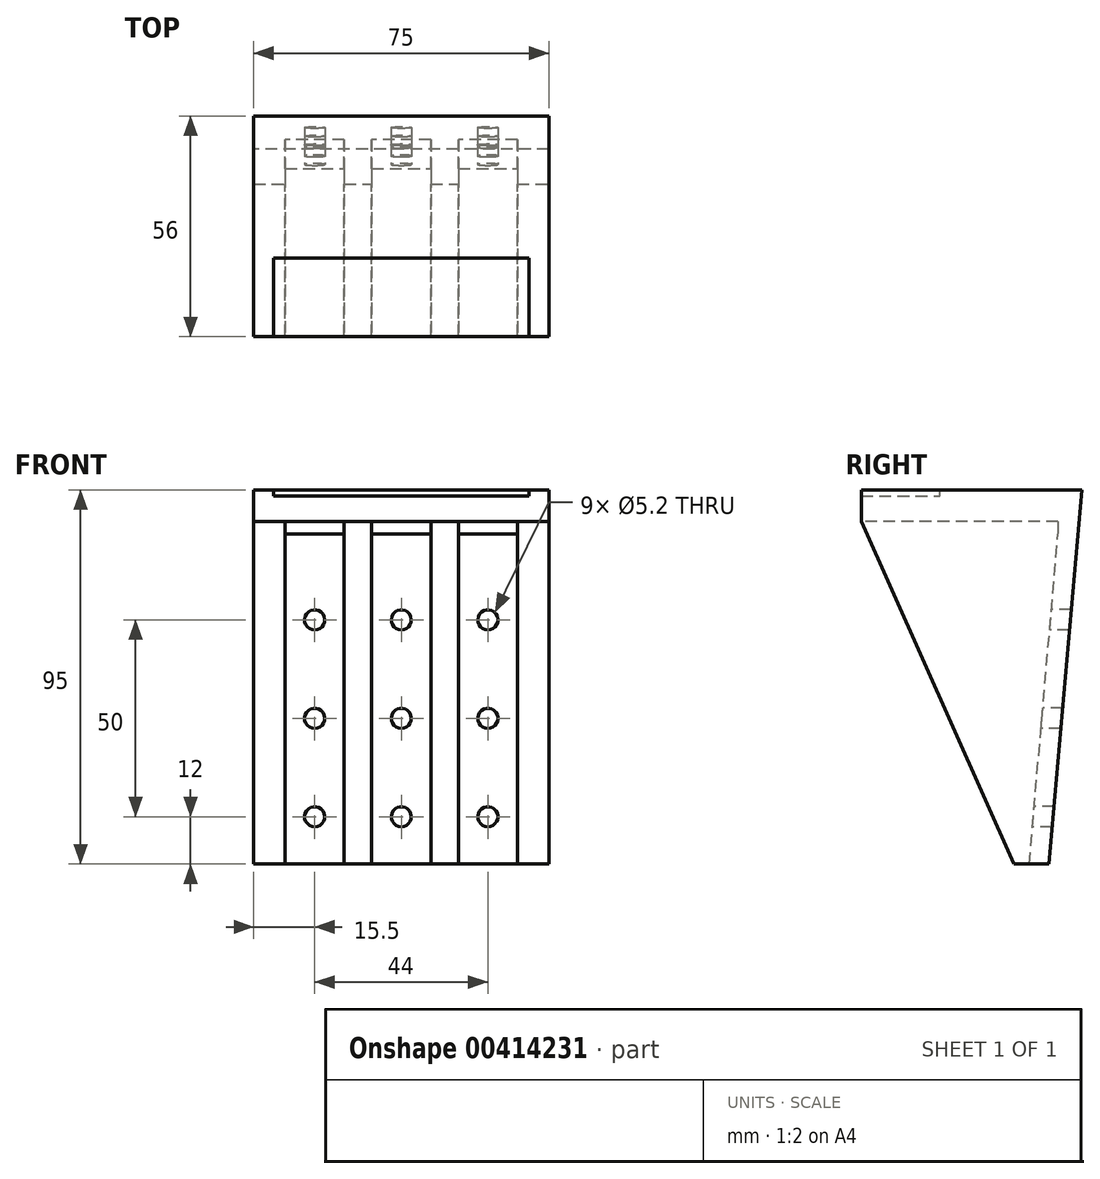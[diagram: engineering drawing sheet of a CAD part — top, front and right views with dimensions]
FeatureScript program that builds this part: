
annotation { "Feature Type Name" : "Feature", "Feature Type Description" : "" }
export const myFeature = defineFeature(function(context is Context, id is Id, definition is map)
    precondition{}
    {
        {
            var Q0;
            Q0=qCreatedBy(makeId("Front.planeOp"),FACE);
            var sketch = newSketch(context, id + "F0", { "sketchPlane" : qUnion([Q0])});
            skLineSegment(sketch, "E0.bottom", {"start": v(0, 0) * mm, "end": v(75, 0) * mm});
            skLineSegment(sketch, "E0.top", {"start": v(0, 100) * mm, "end": v(75, 100) * mm});
            skLineSegment(sketch, "E0.left", {"start": v(0, 0) * mm, "end": v(0, 100) * mm});
            skLineSegment(sketch, "E0.right", {"start": v(75, 0) * mm, "end": v(75, 100) * mm});
            skSolve(sketch);
        }
        {
            var Q0;
            Q0=makeQuery(id+"F0.imprint","IMPRINT",FACE,{"disambiguationData":[TD([[makeQuery(id+"F0.imprint","IMPRINT",EDGE,{"derivedFrom":sQuery(id+"F0.wireOp",EDGE,"E0.bottom")}),1.0]])]});
            extrude(context, id + "F1", {"entities" : qUnion([Q0]), "depth" : 56 * mm});
        }
        {
            var Q0;
            Q0=makeQuery(id+"F1.opExtrude","SWEPT_FACE",FACE,{"disambiguationData":[OSD([sQuery(id+"F0.wireOp",EDGE,"E0.left")])]});
            var sketch = newSketch(context, id + "F2", { "sketchPlane" : qUnion([Q0])});
            skLineSegment(sketch, "E1", {"start": v(15, 0) * mm, "end": v(56, 92) * mm});
            skLineSegment(sketch, "E2", {"start": v(56, 92) * mm, "end": v(56, 0) * mm});
            skLineSegment(sketch, "E3", {"start": v(56, 0) * mm, "end": v(15, 0) * mm});
            skSolve(sketch);
        }
        {
            var Q0;
            Q0=makeQuery(id+"F2.imprint","IMPRINT",FACE,{"disambiguationData":[TD([[makeQuery(id+"F2.imprint","IMPRINT",EDGE,{"derivedFrom":sQuery(id+"F2.wireOp",EDGE,"E1")}),-1.0]])]});
            extrude(context, id + "F3", {"entities" : qUnion([Q0]), "operationType" : NewBodyOperationType.REMOVE, "endBound" : BoundingType.THROUGH_ALL, "oppositeDirection" : true, "depth" : 25 * mm});
        }
        {
            var Q0;
            Q0=makeQuery(id+"F1.opExtrude","CAP_FACE",FACE,{"disambiguationData":[OSD([sQuery(id+"F0.wireOp",EDGE,"E0.bottom"),sQuery(id+"F0.wireOp",EDGE,"E0.top"),sQuery(id+"F0.wireOp",EDGE,"E0.left"),sQuery(id+"F0.wireOp",EDGE,"E0.right")])],"isStart":false});
            var sketch = newSketch(context, id + "F4", { "sketchPlane" : qUnion([Q0])});
            skLineSegment(sketch, "E4.bottom", {"start": v(8, 92) * mm, "end": v(23, 92) * mm});
            skLineSegment(sketch, "E4.top", {"start": v(8, 0) * mm, "end": v(23, 0) * mm});
            skLineSegment(sketch, "E4.left", {"start": v(8, 92) * mm, "end": v(8, 0) * mm});
            skLineSegment(sketch, "E4.right", {"start": v(23, 92) * mm, "end": v(23, 0) * mm});
            skLineSegment(sketch, "E5.bottom", {"start": v(30, 92) * mm, "end": v(45, 92) * mm});
            skLineSegment(sketch, "E5.top", {"start": v(30, 0) * mm, "end": v(45, 0) * mm});
            skLineSegment(sketch, "E5.left", {"start": v(30, 92) * mm, "end": v(30, 0) * mm});
            skLineSegment(sketch, "E5.right", {"start": v(45, 92) * mm, "end": v(45, 0) * mm});
            skLineSegment(sketch, "E6.bottom", {"start": v(52, 92) * mm, "end": v(67, 92) * mm});
            skLineSegment(sketch, "E6.top", {"start": v(52, 0) * mm, "end": v(67, 0) * mm});
            skLineSegment(sketch, "E6.left", {"start": v(52, 92) * mm, "end": v(52, 0) * mm});
            skLineSegment(sketch, "E6.right", {"start": v(67, 92) * mm, "end": v(67, 0) * mm});
            skSolve(sketch);
        }
        {
            var Q0;
            Q0=makeQuery(id+"F4.imprint","IMPRINT",FACE,{"disambiguationData":[TD([[makeQuery(id+"F4.imprint","IMPRINT",EDGE,{"derivedFrom":sQuery(id+"F4.wireOp",EDGE,"E4.bottom")}),1.0]])]});
            var Q1;
            Q1=makeQuery(id+"F4.imprint","IMPRINT",FACE,{"disambiguationData":[TD([[makeQuery(id+"F4.imprint","IMPRINT",EDGE,{"derivedFrom":sQuery(id+"F4.wireOp",EDGE,"E5.bottom")}),1.0]])]});
            var Q2;
            Q2=makeQuery(id+"F4.imprint","IMPRINT",FACE,{"disambiguationData":[TD([[makeQuery(id+"F4.imprint","IMPRINT",EDGE,{"derivedFrom":sQuery(id+"F4.wireOp",EDGE,"E6.bottom")}),1.0]])]});
            extrude(context, id + "F5", {"entities" : qUnion([Q0, Q1, Q2]), "operationType" : NewBodyOperationType.REMOVE, "oppositeDirection" : true, "depth" : 50 * mm});
        }
        {
            var Q0;
            Q0=makeQuery(id+"F1.opExtrude","SWEPT_FACE",FACE,{"disambiguationData":[OSD([sQuery(id+"F0.wireOp",EDGE,"E0.top")])]});
            var sketch = newSketch(context, id + "F6", { "sketchPlane" : qUnion([Q0])});
            skLineSegment(sketch, "E7.bottom", {"start": v(5, -56) * mm, "end": v(70, -56) * mm});
            skLineSegment(sketch, "E7.top", {"start": v(5, -36) * mm, "end": v(70, -36) * mm});
            skLineSegment(sketch, "E7.left", {"start": v(5, -56) * mm, "end": v(5, -36) * mm});
            skLineSegment(sketch, "E7.right", {"start": v(70, -56) * mm, "end": v(70, -36) * mm});
            skSolve(sketch);
        }
        {
            var Q0;
            Q0=makeQuery(id+"F6.imprint","IMPRINT",FACE,{"disambiguationData":[TD([[makeQuery(id+"F6.imprint","IMPRINT",EDGE,{"derivedFrom":sQuery(id+"F6.wireOp",EDGE,"E7.bottom")}),1.0]])]});
            extrude(context, id + "F7", {"entities" : qUnion([Q0]), "operationType" : NewBodyOperationType.REMOVE, "oppositeDirection" : true, "depth" : 1.5 * mm});
        }
        {
            var Q0;
            Q0=makeQuery(id+"F1.opExtrude","SWEPT_FACE",FACE,{"disambiguationData":[OSD([sQuery(id+"F0.wireOp",EDGE,"E0.left")])]});
            var sketch = newSketch(context, id + "F8", { "sketchPlane" : qUnion([Q0])});
            skLineSegment(sketch, "E8", {"start": v(0, 100) * mm, "end": v(8.75, 0) * mm});
            skLineSegment(sketch, "E9", {"start": v(8.75, 0) * mm, "end": v(0, 0) * mm});
            skLineSegment(sketch, "E10", {"start": v(0, 0) * mm, "end": v(0, 100) * mm});
            skSolve(sketch);
        }
        {
            var Q0;
            Q0=makeQuery(id+"F8.imprint","IMPRINT",FACE,{"disambiguationData":[TD([[makeQuery(id+"F8.imprint","IMPRINT",EDGE,{"derivedFrom":sQuery(id+"F8.wireOp",EDGE,"E8")}),-1.0]])]});
            extrude(context, id + "F9", {"entities" : qUnion([Q0]), "operationType" : NewBodyOperationType.REMOVE, "endBound" : BoundingType.THROUGH_ALL, "oppositeDirection" : true, "depth" : 25 * mm});
        }
        {
            var Q0;
            Q0=makeQuery(id+"F1.opExtrude","SWEPT_FACE",FACE,{"disambiguationData":[OSD([sQuery(id+"F0.wireOp",EDGE,"E0.left")])]});
            var sketch = newSketch(context, id + "F10", { "sketchPlane" : qUnion([Q0])});
            skLineSegment(sketch, "E11", {"start": v(0, 100) * mm, "end": v(8.75, 0) * mm});
            skLineSegment(sketch, "E12", {"start": v(8.75, 0) * mm, "end": v(13.77, 0) * mm});
            skLineSegment(sketch, "E13", {"start": v(13.77, 0) * mm, "end": v(5.02, 100) * mm});
            skLineSegment(sketch, "E14", {"start": v(5.02, 100) * mm, "end": v(0, 100) * mm});
            skSolve(sketch);
        }
        {
            var Q0;
            Q0=makeQuery(id+"F10.imprint","IMPRINT",FACE,{"disambiguationData":[TD([[makeQuery(id+"F10.imprint","IMPRINT",EDGE,{"derivedFrom":sQuery(id+"F10.wireOp",EDGE,"E11")}),1.0]])]});
            var Q1;
            Q1=makeQuery(id+"F1.opExtrude","SWEPT_FACE",FACE,{"disambiguationData":[OSD([sQuery(id+"F0.wireOp",EDGE,"E0.right")])]});
            extrude(context, id + "F11", {"entities" : qUnion([Q0]), "operationType" : NewBodyOperationType.ADD, "endBound" : BoundingType.UP_TO_SURFACE, "oppositeDirection" : true, "endBoundEntityFace" : qUnion([Q1]), "depth" : 25 * mm});
        }
        {
            var Q0;
            Q0=makeQuery(id+"F1.opExtrude","CAP_FACE",FACE,{"disambiguationData":[OSD([sQuery(id+"F0.wireOp",EDGE,"E0.bottom"),sQuery(id+"F0.wireOp",EDGE,"E0.top"),sQuery(id+"F0.wireOp",EDGE,"E0.left"),sQuery(id+"F0.wireOp",EDGE,"E0.right")])],"isStart":false});
            var sketch = newSketch(context, id + "F12", { "sketchPlane" : qUnion([Q0])});
            skLineSegment(sketch, "E15", {"start": v(15.5, 92) * mm, "end": v(15.5, 0) * mm, "construction": true});
            skLineSegment(sketch, "E16", {"start": v(37.5, 92) * mm, "end": v(37.5, 0) * mm, "construction": true});
            skLineSegment(sketch, "E17", {"start": v(59.5, 92) * mm, "end": v(59.5, 0) * mm, "construction": true});
            skLineSegment(sketch, "E18.bottom", {"start": v(0, 0) * mm, "end": v(75, 0) * mm});
            skLineSegment(sketch, "E18.top", {"start": v(0, 5) * mm, "end": v(75, 5) * mm});
            skLineSegment(sketch, "E18.left", {"start": v(0, 0) * mm, "end": v(0, 5) * mm});
            skLineSegment(sketch, "E18.right", {"start": v(75, 0) * mm, "end": v(75, 5) * mm});
            skCircle(sketch, "E19", {"center": v(15.5, 17) * mm, "radius": 2.6 * mm});
            skCircle(sketch, "E20", {"center": v(15.5, 42) * mm, "radius": 2.6 * mm});
            skCircle(sketch, "E21", {"center": v(15.5, 67) * mm, "radius": 2.6 * mm});
            skCircle(sketch, "E22", {"center": v(37.5, 67) * mm, "radius": 2.6 * mm});
            skCircle(sketch, "E23", {"center": v(37.5, 42) * mm, "radius": 2.6 * mm});
            skCircle(sketch, "E24", {"center": v(37.5, 17) * mm, "radius": 2.6 * mm});
            skCircle(sketch, "E25", {"center": v(59.5, 17) * mm, "radius": 2.6 * mm});
            skCircle(sketch, "E26", {"center": v(59.5, 42) * mm, "radius": 2.6 * mm});
            skCircle(sketch, "E27", {"center": v(59.5, 67) * mm, "radius": 2.6 * mm});
            skSolve(sketch);
        }
        {
            var Q0;
            Q0 = qSketchRegion(id + "F12", true);
            extrude(context, id + "F13", {"entities" : qUnion([Q0]), "operationType" : NewBodyOperationType.REMOVE, "endBound" : BoundingType.THROUGH_ALL, "oppositeDirection" : true, "depth" : 25 * mm});
        }
    });
